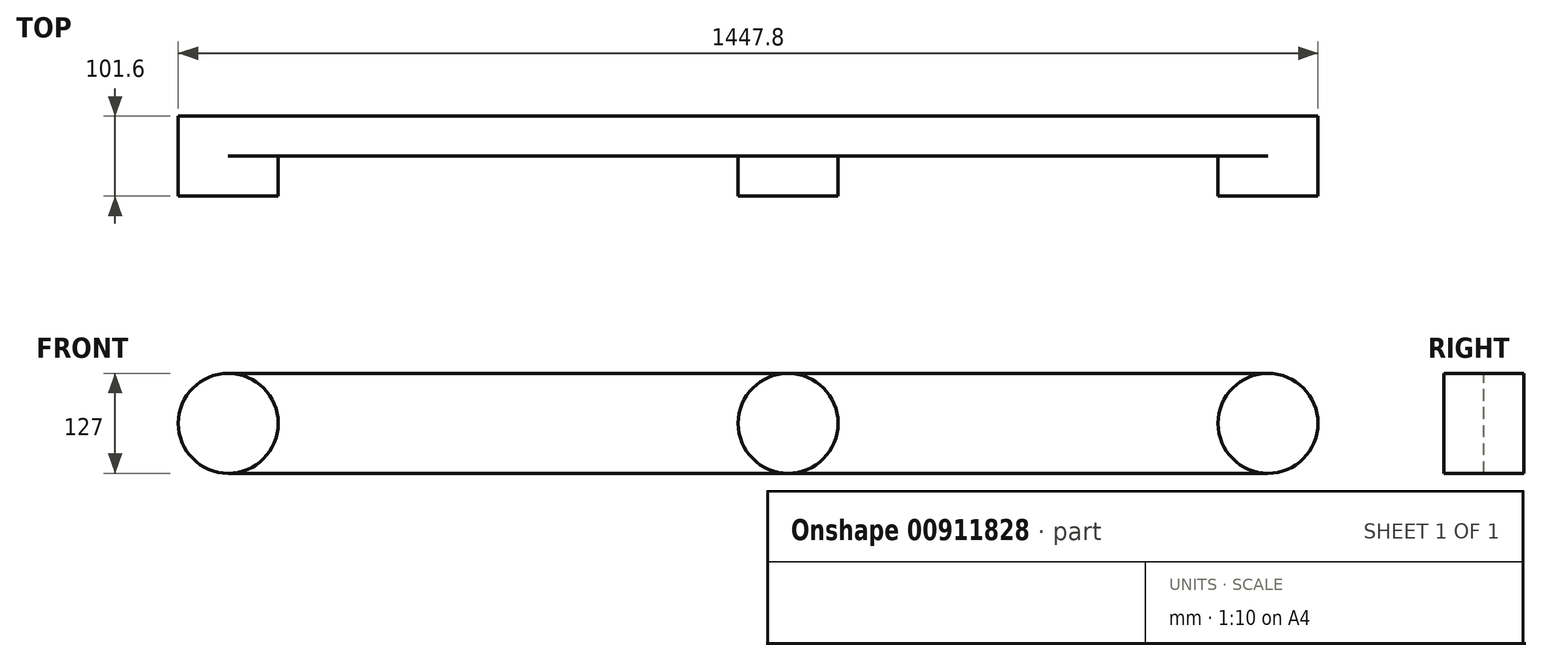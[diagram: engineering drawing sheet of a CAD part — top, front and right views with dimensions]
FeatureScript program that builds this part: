
annotation { "Feature Type Name" : "Feature", "Feature Type Description" : "" }
export const myFeature = defineFeature(function(context is Context, id is Id, definition is map)
    precondition{}
    {
        {
            var Q0;
            Q0=qCreatedBy(makeId("Front.planeOp"),FACE);
            var sketch = newSketch(context, id + "F0", { "sketchPlane" : qUnion([Q0])});
            skLineSegment(sketch, "E0.bottom", {"start": v(0, 0) * mm, "end": v(1320.8, 0) * mm});
            skLineSegment(sketch, "E0.top", {"start": v(0, 127) * mm, "end": v(1320.8, 127) * mm});
            skArc(sketch, "E1", {"start": v(0, 127) * mm, "mid": v(-63.5, 63.5) * mm, "end": v(0, 0) * mm});
            skArc(sketch, "E2", {"start": v(1320.8, 0) * mm, "mid": v(1384.3, 63.5) * mm, "end": v(1320.8, 127) * mm});
            skSolve(sketch);
        }
        {
            var Q0;
            Q0 = qSketchRegion(id + "F0", true);
            extrude(context, id + "F1", {"entities" : qUnion([Q0]), "depth" : 50.8 * mm, "offsetDistance" : 25 * mm});
        }
        {
            var Q0;
            Q0=makeQuery(id+"F1.opExtrude","CAP_FACE",FACE,{"disambiguationData":[OSD([sQuery(id+"F0.wireOp",EDGE,"E0.bottom"),sQuery(id+"F0.wireOp",EDGE,"E0.top"),sQuery(id+"F0.wireOp",EDGE,"E1"),sQuery(id+"F0.wireOp",EDGE,"E2")])],"isStart":false});
            var sketch = newSketch(context, id + "F2", { "sketchPlane" : qUnion([Q0])});
            skCircle(sketch, "E3", {"center": v(0, 63.5) * mm, "radius": 63.5 * mm});
            skCircle(sketch, "E4", {"center": v(1320.8, 63.5) * mm, "radius": 63.5 * mm});
            skCircle(sketch, "E5", {"center": v(711.2, 63.5) * mm, "radius": 63.5 * mm});
            skSolve(sketch);
        }
        {
            var Q0;
            Q0 = qSketchRegion(id + "F2", true);
            extrude(context, id + "F3", {"entities" : qUnion([Q0]), "operationType" : NewBodyOperationType.ADD, "depth" : 50.8 * mm, "offsetDistance" : 25 * mm});
        }
    });
